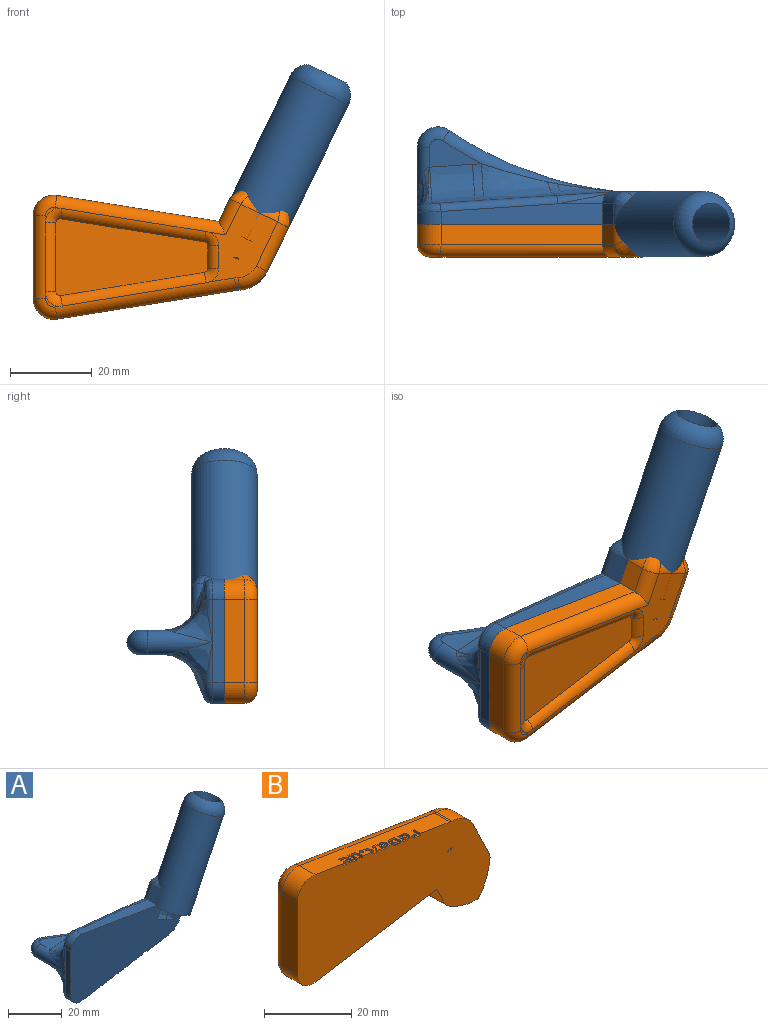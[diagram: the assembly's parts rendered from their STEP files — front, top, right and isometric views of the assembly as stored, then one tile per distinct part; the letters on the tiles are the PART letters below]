
ASSEMBLY  parts=2 mates=1
PART A: 139 faces, bbox 79.2x33.1x63.6 mm
  f0: plane 59.38x33.12mm, normal (0,-1,0), area 1204.5mm2, adj f1,f2,f3,f10,f11,f12,f17,f18
  f1: plane 43.87x7.02mm, normal (0.16,0,-0.99), area 174.7mm2, adj f0,f12,f14,f21,f29,f70,f71,f72
  f2: plane 0.98x0.28mm, normal (0.16,0,-0.99), area 0.2mm2, adj f0,f79,f80,f81,f82
  f3: plane 1.13x0.48mm, normal (0.16,0,-0.99), area 0.4mm2, adj f0,f74,f75,f76,f77
  f4: plane 13.96x9.51mm, normal (-0.07,1,0), area 24.1mm2, adj f28,f30,f32,f45
  f5: plane 10.96x6.39mm, normal (-0.07,1,0), area 12.6mm2, adj f9,f31,f33,f55
  f6: plane 18.19x10.63mm, normal (0,1,0), area 119mm2, adj f9,f13,f15,f22,f23,f32,f49,f51
  f7: plane 8.12x0.95mm, normal (-0.07,1,0), area 4.2mm2, adj f27,f29,f52,f54
  f8: cylinder r=2mm len=20.37mm, axis (0,0,-1), area 22.6mm2, adj f11,f25,f27,f46,f48
  f9: cylinder r=2mm len=3.69mm, axis (0,0,-1), area 0.4mm2, adj f5,f6,f33,f53
  f10: cylinder r=5mm len=5.8mm, axis (0,1,0), area 26mm2, adj f0,f11,f20,f25
  f11: plane 20.37x2.88mm, normal (-1,0,0), area 58.7mm2, adj f0,f8,f10,f12
  f12: cylinder r=5mm len=5.79mm, axis (0,1,0), area 25.9mm2, adj f0,f1,f11,f27
  f13: torus R=8mm, axis (0,-1,0), area 3.6mm2, adj f6,f14,f21,f23,f33
  f14: cylinder r=3mm len=15.67mm, axis (0.99,0,0.16), area 26.4mm2, adj f1,f13,f31
  f15: cylinder r=3mm len=7.86mm, axis (-0.44,0,-0.9), area 27.9mm2, adj f6,f16,f19,f28,f30,f60
  f16: cylinder r=3mm len=11.93mm, axis (-0.99,0,0.16), area 14.6mm2, adj f15,f20,f28
  f17: cylinder r=8mm len=6.92mm, axis (0,1,0), area 43.3mm2, adj f0,f18,f21,f23
  f18: plane 10.79x5.26mm, normal (0.9,0,-0.44), area 60mm2, adj f0,f17,f22,f63,f64
  f19: plane 5.54x5mm, normal (-0.9,0,0.44), area 30.8mm2, adj f15,f20,f59,f64
  f20: plane 39.57x6.41mm, normal (0.16,0,0.99), area 173.1mm2, adj f0,f10,f16,f19,f26
  f21: cylinder r=5mm len=5mm, axis (0,1,0), area 3.1mm2, adj f0,f1,f13,f17
  f22: cylinder r=3mm len=12.1mm, axis (0.44,0,0.9), area 56.5mm2, adj f6,f18,f23,f62
  f23: torus R=5mm, axis (0,-1,0), area 35.3mm2, adj f6,f13,f17,f22
  f24: plane 11.83x1.53mm, normal (-0.07,1,0), area 9.6mm2, adj f25,f26,f40,f42
  f25: bspline ~6.51x5.22mm, area 22mm2, adj f8,f10,f24,f26,f44
  f26: cylinder r=2mm len=29.07mm, axis (0.99,0.06,-0.16), area 91.9mm2, adj f20,f24,f25,f28,f39,f41
  f27: bspline ~6.51x5.87mm, area 21.3mm2, adj f7,f8,f12,f29,f50
  f28: bspline ~18.15x6.04mm, area 28.9mm2, adj f4,f15,f16,f26,f30,f43
  f29: cylinder r=2mm len=29.07mm, axis (0.99,0.06,0.16), area 91.9mm2, adj f1,f7,f27,f31,f56,f58
  f30: bspline ~4.02x3.48mm, area 2.9mm2, adj f4,f15,f28,f32
  f31: bspline ~17.8x6.19mm, area 31.6mm2, adj f5,f14,f29,f33,f57
  f32: cylinder r=2mm len=8.96mm, axis (0,0,-1), area 1.1mm2, adj f4,f6,f30,f47
  f33: bspline ~0.55x0.32mm, area 0mm2, adj f5,f9,f13,f31
  f34: plane 12.78x6.91mm, normal (0,0,-1), area 49mm2, adj f36,f37,f38,f54,f56
  f35: plane 12.67x6.86mm, normal (0,0,1), area 48.9mm2, adj f36,f37,f38,f39,f40
  f36: torus R=91.5mm, axis (0,0,1), area 273.7mm2, adj f34,f35,f37,f41,f43,f45,f47,f49
  f37: torus R=2mm, axis (0,0,1), area 79.9mm2, adj f34,f35,f36,f38
  f38: cylinder r=3mm len=15.5mm, axis (0,1,0), area 82.4mm2, adj f34,f35,f37,f42,f44,f46,f48,f50
  f39: bspline ~9.12x9mm, area 29.9mm2, adj f26,f35,f40,f41
  f40: bspline ~13.25x9.82mm, area 147.7mm2, adj f24,f35,f39,f42
  f41: bspline ~18.28x9.37mm, area 170.8mm2, adj f26,f36,f39,f43
  f42: bspline ~9.07x9.02mm, area 10mm2, adj f24,f38,f40,f44
  f43: bspline ~6.69x4.69mm, area 18.2mm2, adj f28,f36,f41,f45
  f44: bspline ~9.31x9.21mm, area 9.7mm2, adj f25,f38,f42,f46
  f45: bspline ~20.74x9.64mm, area 66.6mm2, adj f4,f36,f43,f47
  f46: bspline ~10.45x9.78mm, area 44.9mm2, adj f8,f38,f44,f48
  f47: bspline ~1.74x1.66mm, area 1.2mm2, adj f32,f36,f45,f49
  f48: bspline ~9.91x9.29mm, area 41.2mm2, adj f8,f38,f46,f50
  f49: bspline ~1.5x1.17mm, area 1mm2, adj f6,f36,f47,f51
  f50: bspline ~9.49x9.33mm, area 16.1mm2, adj f27,f38,f48,f52
  f51: bspline ~1.5x1.17mm, area 1mm2, adj f6,f36,f49,f53
  f52: bspline ~9.04x9.01mm, area 6.8mm2, adj f7,f38,f50,f54
  f53: bspline ~1.74x1.66mm, area 1.2mm2, adj f9,f36,f51,f55
  f54: bspline ~13.25x9.82mm, area 101.4mm2, adj f7,f34,f52,f56
  f55: bspline ~20.69x9.63mm, area 47.8mm2, adj f5,f36,f53,f57
  f56: bspline ~9.3x9mm, area 74.3mm2, adj f29,f34,f54,f58
  f57: bspline ~7.28x6.44mm, area 34.3mm2, adj f31,f36,f55,f58
  f58: bspline ~18.22x8.95mm, area 163mm2, adj f29,f36,f56,f57
  f59: bspline ~10.7x7.19mm, area 5.6mm2, adj f19,f60,f64
  f60: bspline ~4.49x3.76mm, area 13.9mm2, adj f15,f59,f61,f64
  f61: bspline ~12.5x11.57mm, area 11.6mm2, adj f6,f60,f62,f64
  f62: bspline ~3.91x3.76mm, area 13.9mm2, adj f22,f61,f63,f64
  f63: bspline ~10.7x7.19mm, area 5.6mm2, adj f18,f62,f64
  f64: cylinder r=8mm len=43.38mm, axis (0.44,0,0.9), area 1816.7mm2, adj f0,f18,f19,f59,f60,f61,f62,f63
  f65: plane 14.38x8mm, normal (-0.44,0,-0.9), area 59.7mm2, adj f0,f64,f66
  f66: cylinder r=5.1mm len=49.41mm, axis (0.44,0,0.9), area 1522.1mm2, adj f0,f65,f68,f69
  f67: cylinder r=0.02mm len=17.99mm, axis (0.44,0,0.9), area 1mm2, adj f0,f68
  f68: plane 9.17x5.1mm, normal (0.44,0,0.9), area 40.8mm2, adj f0,f66,f67
  f69: torus R=3mm, axis (0.44,0,0.9), area 249.7mm2, adj f64,f66
  f70: extruded ~0.7x0.55mm, area 0.4mm2, adj f0,f1,f71,f78
  f71: extruded ~1.07x0.65mm, area 0.5mm2, adj f1,f70,f72,f78
  f72: extruded ~1.12x0.66mm, area 0.6mm2, adj f1,f71,f73,f78
  f73: extruded ~0.65x0.55mm, area 0.4mm2, adj f0,f1,f72,f78
  f74: extruded ~0.56x0.49mm, area 0.2mm2, adj f3,f75,f77,f78
  f75: extruded ~0.56x0.49mm, area 0.2mm2, adj f3,f74,f76,f78
  f76: extruded ~0.52x0.31mm, area 0.2mm2, adj f0,f3,f75,f78
  f77: extruded ~0.52x0.31mm, area 0.2mm2, adj f0,f3,f74,f78
  f78: plane 2.72x1.09mm, normal (0.16,0,-0.99), area 1.8mm2, adj f0,f70,f71,f72,f73,f74,f75,f76
  f79: extruded ~0.5x0.11mm, area 0mm2, adj f0,f2,f80,f91
  f80: extruded ~0.56x0.5mm, area 0.3mm2, adj f2,f79,f81,f91
  f81: extruded ~0.57x0.56mm, area 0.3mm2, adj f2,f80,f82,f91
  f82: extruded ~0.5x0.12mm, area 0mm2, adj f0,f2,f81,f91
  f83: plane 2.08x0.49mm, normal (0.99,0,0.16), area 1mm2, adj f0,f1,f84,f91
  f84: plane 0.9x0.63mm, normal (0,-1,0), area 0.4mm2, adj f1,f83,f85,f91
  f85: plane 0.97x0.49mm, normal (-0.99,0,-0.16), area 0.5mm2, adj f1,f84,f86,f91
  f86: extruded ~0.61x0.5mm, area 0.3mm2, adj f1,f85,f87,f91
  f87: plane 0.5x0.11mm, normal (0,-1,0), area 0mm2, adj f1,f86,f88,f91
  f88: extruded ~0.94x0.63mm, area 0.5mm2, adj f1,f87,f89,f91
  f89: extruded ~0.92x0.63mm, area 0.5mm2, adj f1,f88,f90,f91
  f90: extruded ~0.54x0.53mm, area 0.3mm2, adj f0,f1,f89,f91
  f91: plane 2.74x2.1mm, normal (0.16,0,-0.99), area 3mm2, adj f0,f79,f80,f81,f82,f83,f84,f85
  f92: plane 1.97x1.31mm, normal (0.83,0.53,0.13), area 1.2mm2, adj f0,f1,f93,f99
  f93: plane 0.97x0.64mm, normal (0,-1,0), area 0.5mm2, adj f1,f92,f94,f99
  f94: plane 1.43x0.91mm, normal (-0.85,-0.51,-0.14), area 0.8mm2, adj f1,f93,f95,f99
  f95: plane 1.43x0.92mm, normal (0.85,-0.51,0.14), area 0.8mm2, adj f1,f94,f96,f99
  f96: plane 1x0.64mm, normal (0,-1,0), area 0.5mm2, adj f1,f95,f97,f99
  f97: plane 1.92x1.3mm, normal (-0.83,0.54,-0.13), area 1.1mm2, adj f1,f96,f98,f99
  f98: plane 0.5x0.11mm, normal (-0.83,-0.54,-0.13), area 0mm2, adj f0,f1,f97,f99
  f99: plane 3.48x1.97mm, normal (0.16,0,-0.99), area 3.3mm2, adj f0,f92,f93,f94,f95,f96,f97,f98
  f100: extruded ~0.8x0.55mm, area 0.4mm2, adj f0,f1,f101,f106
  f101: extruded ~1x0.64mm, area 0.5mm2, adj f1,f100,f102,f106
  f102: extruded ~1.23x0.68mm, area 0.6mm2, adj f1,f101,f103,f106
  f103: plane 0.56x0.54mm, normal (-0.89,0.44,-0.14), area 0.3mm2, adj f1,f102,f104,f106
  f104: extruded ~0.92x0.63mm, area 0.4mm2, adj f1,f103,f105,f106
  f105: extruded ~0.57x0.55mm, area 0.4mm2, adj f0,f1,f104,f106
  f106: plane 2.39x1.07mm, normal (0.16,0,-0.99), area 1.6mm2, adj f0,f100,f101,f102,f103,f104,f105
  f107: plane 0.57x0.56mm, normal (0,-1,0), area 0.2mm2, adj f108,f120,f122,f123
  f108: plane 0.88x0.49mm, normal (0.99,0,0.16), area 0.4mm2, adj f107,f109,f122,f123
  f109: plane 0.56x0.52mm, normal (0,1,0), area 0.2mm2, adj f108,f110,f122,f123
  f110: extruded ~0.6x0.58mm, area 0.3mm2, adj f109,f111,f122,f123
  f111: extruded ~0.52x0.33mm, area 0.2mm2, adj f110,f112,f122,f123
  f112: extruded ~0.52x0.35mm, area 0.2mm2, adj f111,f120,f122,f123
  f113: plane 1.3x0.69mm, normal (0,-1,0), area 0.6mm2, adj f1,f114,f121,f122
  f114: plane 1.97x0.49mm, normal (-0.99,0,-0.16), area 1mm2, adj f0,f1,f113,f122
  f115: extruded ~0.53x0.32mm, area 0.1mm2, adj f0,f1,f116,f122
  f116: plane 0.49x0.08mm, normal (0.99,0,0.16), area 0mm2, adj f1,f115,f117,f122
  f117: extruded ~0.56x0.52mm, area 0.3mm2, adj f1,f116,f118,f122
  f118: extruded ~0.58x0.52mm, area 0.3mm2, adj f1,f117,f119,f122
  f119: extruded ~0.76x0.55mm, area 0.4mm2, adj f1,f118,f121,f122
  f120: extruded ~0.57x0.57mm, area 0.3mm2, adj f107,f112,f122,f123
  f121: extruded ~1.29x0.69mm, area 0.6mm2, adj f1,f113,f119,f122
  f122: plane 2.8x1.97mm, normal (0.16,0,-0.99), area 4.3mm2, adj f0,f107,f108,f109,f110,f111,f112,f113
  f123: plane 1.12x0.88mm, normal (0.16,0,-0.99), area 0.9mm2, adj f107,f108,f109,f110,f111,f112,f120
  f124: extruded ~0.8x0.55mm, area 0.4mm2, adj f0,f1,f125,f130
  f125: extruded ~1x0.64mm, area 0.5mm2, adj f1,f124,f126,f130
  f126: extruded ~1.23x0.68mm, area 0.6mm2, adj f1,f125,f127,f130
  f127: plane 0.56x0.54mm, normal (-0.89,0.44,-0.14), area 0.3mm2, adj f1,f126,f128,f130
  f128: extruded ~0.92x0.63mm, area 0.4mm2, adj f1,f127,f129,f130
  f129: extruded ~0.57x0.55mm, area 0.4mm2, adj f0,f1,f128,f130
  f130: plane 2.39x1.07mm, normal (0.16,0,-0.99), area 1.6mm2, adj f0,f124,f125,f126,f127,f128,f129
  f131: plane 0.49x0.25mm, normal (0.99,0,0.16), area 0.1mm2, adj f0,f1,f132,f138
  f132: plane 1.41x0.71mm, normal (0,-1,0), area 0.7mm2, adj f1,f131,f133,f138
  f133: plane 1.02x0.49mm, normal (0.99,0,0.16), area 0.5mm2, adj f1,f132,f134,f138
  f134: plane 1.51x0.72mm, normal (0,1,0), area 0.7mm2, adj f1,f133,f135,f138
  f135: plane 0.69x0.49mm, normal (0.99,0,0.16), area 0.3mm2, adj f1,f134,f136,f138
  f136: plane 2.32x0.85mm, normal (0,-1,0), area 1.1mm2, adj f1,f135,f137,f138
  f137: plane 1.97x0.49mm, normal (-0.99,0,-0.16), area 1mm2, adj f0,f1,f136,f138
  f138: plane 2.25x1.97mm, normal (0.16,0,-0.99), area 3mm2, adj f0,f131,f132,f133,f134,f135,f136,f137
PART B: 157 faces, bbox 68x10.3x38.8 mm
  f0: plane 43.85x7.11mm, normal (0.16,0,0.99), area 191.2mm2, adj f3,f11,f12,f21,f36,f37,f38,f39
  f1: plane 1.15x0.19mm, normal (0.16,0,0.99), area 0.2mm2, adj f3,f48,f49,f50
  f2: plane 1.55x1.21mm, normal (0.16,0,0.99), area 1.7mm2, adj f3,f53,f54,f55,f56,f57,f58,f67
  f3: plane 64.71x35.47mm, normal (0,-1,0), area 1448.9mm2, adj f0,f1,f2,f7,f8,f9,f10,f11
  f4: plane 3.23x2.92mm, normal (0,1,0), area 2mm2, adj f23,f25,f26,f34
  f5: plane 19.06x16.66mm, normal (0,1,0), area 170.7mm2, adj f7,f8,f17,f18,f19,f20,f21,f24
  f6: plane 3.24x2.93mm, normal (0,1,0), area 2.1mm2, adj f21,f22,f23,f30
  f7: plane 8x1.31mm, normal (0.39,0,-0.92), area 11.4mm2, adj f3,f5,f8,f17
  f8: plane 8x0.56mm, normal (-0.9,0,0.44), area 5mm2, adj f3,f5,f7,f17
  f9: plane 10.79x5.26mm, normal (0.9,0,0.44), area 60mm2, adj f3,f10,f18,f152
  f10: cylinder r=8mm len=6.91mm, axis (0,1,0), area 43.3mm2, adj f3,f9,f11,f19
  f11: cylinder r=5mm len=5mm, axis (0,1,0), area 3.2mm2, adj f0,f3,f10,f20
  f12: cylinder r=5mm len=5.8mm, axis (0,1,0), area 43.3mm2, adj f0,f3,f13,f22
  f13: plane 20.37x5mm, normal (-1,0,0), area 101.8mm2, adj f3,f12,f14,f23
  f14: cylinder r=5mm len=5.79mm, axis (0,1,0), area 43.2mm2, adj f3,f13,f15,f25
  f15: plane 39.57x6.33mm, normal (0.16,0,-0.99), area 200.4mm2, adj f3,f14,f16,f26
  f16: plane 5.55x5mm, normal (-0.9,0,-0.44), area 30.9mm2, adj f3,f15,f24,f156
  f17: plane 8x1.04mm, normal (0,0,1), area 8.3mm2, adj f3,f5,f7,f8
  f18: cylinder r=3mm len=12.1mm, axis (-0.44,0,0.9), area 56.5mm2, adj f5,f9,f19,f153
  f19: torus R=5mm, axis (0,-1,0), area 35.2mm2, adj f5,f10,f18,f20
  f20: torus R=8mm, axis (0,-1,0), area 3.6mm2, adj f5,f11,f19,f21
  f21: cylinder r=3mm len=44.33mm, axis (-0.99,0,0.16), area 207.5mm2, adj f0,f5,f6,f20,f22,f28,f29,f30
  f22: torus R=2mm, axis (0,-1,0), area 31.9mm2, adj f6,f12,f21,f23
  f23: cylinder r=3mm len=20.37mm, axis (0,0,-1), area 95.1mm2, adj f4,f6,f13,f22,f25,f30,f32,f34
  f24: cylinder r=3mm len=8.86mm, axis (0.44,0,-0.9), area 34.3mm2, adj f5,f16,f26,f155
  f25: torus R=2mm, axis (0,-1,0), area 31.9mm2, adj f4,f14,f23,f26
  f26: cylinder r=3mm len=42.24mm, axis (0.99,0,0.16), area 190.9mm2, adj f4,f5,f15,f24,f25,f33,f34,f35
  f27: plane 37.22x18.84mm, normal (0,1,0), area 490.3mm2, adj f28,f29,f30,f31,f32,f33,f34,f35
  f28: cylinder r=3mm len=35.63mm, axis (-0.99,0,0.16), area 110.3mm2, adj f21,f27,f29,f30
  f29: torus R=3.6mm, axis (0,-1,0), area 9.6mm2, adj f5,f21,f27,f28,f31
  f30: torus R=3.6mm, axis (0,-1,0), area 11.7mm2, adj f6,f21,f23,f27,f28,f32
  f31: cylinder r=3mm len=5.5mm, axis (0,0,-1), area 17.3mm2, adj f5,f27,f29,f33
  f32: cylinder r=3mm len=16.84mm, axis (0,0,-1), area 52.1mm2, adj f23,f27,f30,f34
  f33: torus R=3.6mm, axis (0,-1,0), area 9.6mm2, adj f5,f26,f27,f31,f35
  f34: torus R=3.6mm, axis (0,-1,0), area 11.7mm2, adj f4,f23,f26,f27,f32,f35
  f35: cylinder r=3mm len=35.63mm, axis (-0.99,0,-0.16), area 110.3mm2, adj f26,f27,f33,f34
  f36: extruded ~1.21x0.68mm, area 0.6mm2, adj f0,f37,f51,f52
  f37: extruded ~0.67x0.59mm, area 0.3mm2, adj f0,f36,f38,f52
  f38: extruded ~0.57x0.54mm, area 0.2mm2, adj f0,f37,f39,f52
  f39: plane 0.64x0.49mm, normal (0.99,0,-0.16), area 0.3mm2, adj f0,f38,f40,f52
  f40: extruded ~0.58x0.58mm, area 0.3mm2, adj f0,f39,f41,f52
  f41: extruded ~0.59x0.58mm, area 0.3mm2, adj f0,f40,f42,f52
  f42: extruded ~0.62x0.58mm, area 0.3mm2, adj f0,f41,f43,f52
  f43: extruded ~0.55x0.53mm, area 0.3mm2, adj f0,f42,f44,f52
  f44: plane 2.01x0.81mm, normal (0,-1,0), area 1mm2, adj f0,f43,f45,f52
  f45: plane 0.49x0.4mm, normal (0.99,0,-0.16), area 0.2mm2, adj f0,f44,f46,f52
  f46: extruded ~0.5x0.32mm, area 0.2mm2, adj f0,f3,f45,f52
  f47: extruded ~0.53x0.5mm, area 0.3mm2, adj f0,f3,f51,f52
  f48: extruded ~0.5x0.17mm, area 0.1mm2, adj f1,f3,f49,f52
  f49: plane 1.23x0.68mm, normal (0,1,0), area 0.6mm2, adj f1,f48,f50,f52
  f50: extruded ~0.5x0.17mm, area 0.1mm2, adj f1,f3,f49,f52
  f51: extruded ~1.15x0.56mm, area 0.6mm2, adj f0,f36,f47,f52
  f52: plane 2.76x2.09mm, normal (0.16,0,0.99), area 3.7mm2, adj f3,f36,f37,f38,f39,f40,f41,f42
  f53: extruded ~0.57x0.54mm, area 0.3mm2, adj f2,f54,f67,f68
  f54: extruded ~0.56x0.52mm, area 0.3mm2, adj f2,f53,f55,f68
  f55: extruded ~0.67x0.52mm, area 0.3mm2, adj f2,f54,f56,f68
  f56: extruded ~0.64x0.51mm, area 0.3mm2, adj f2,f3,f55,f68
  f57: extruded ~0.63x0.51mm, area 0.3mm2, adj f2,f3,f58,f68
  f58: plane 0.49x0.09mm, normal (-0.99,0,0.16), area 0mm2, adj f2,f57,f67,f68
  f59: extruded ~0.91x0.63mm, area 0.5mm2, adj f0,f60,f66,f68
  f60: extruded ~0.93x0.63mm, area 0.5mm2, adj f0,f59,f61,f68
  f61: plane 0.5x0.12mm, normal (0,-1,0), area 0mm2, adj f0,f60,f62,f68
  f62: plane 0.52x0.39mm, normal (-0.91,-0.38,0.15), area 0.2mm2, adj f0,f61,f63,f68
  f63: plane 0.71x0.6mm, normal (0,-1,0), area 0.3mm2, adj f0,f62,f64,f68
  f64: plane 2.14x0.49mm, normal (0.99,0,-0.16), area 1.1mm2, adj f0,f3,f63,f68
  f65: extruded ~0.63x0.5mm, area 0.3mm2, adj f0,f3,f66,f68
  f66: extruded ~1.15x0.54mm, area 0.6mm2, adj f0,f59,f65,f68
  f67: extruded ~0.63x0.52mm, area 0.3mm2, adj f2,f53,f58,f68
  f68: plane 2.8x2.21mm, normal (0.16,0,0.99), area 4mm2, adj f3,f53,f54,f55,f56,f57,f58,f59
  f69: plane 1.03x0.65mm, normal (0,-1,0), area 0.5mm2, adj f0,f70,f75,f76
  f70: plane 2x1.4mm, normal (0.82,0.56,-0.13), area 1.2mm2, adj f0,f69,f71,f76
  f71: plane 0.49x0.08mm, normal (0.83,-0.53,-0.14), area 0mm2, adj f0,f3,f70,f76
  f72: plane 2x1.35mm, normal (-0.83,0.54,0.13), area 1.2mm2, adj f0,f3,f73,f76
  f73: plane 0.97x0.64mm, normal (0,-1,0), area 0.5mm2, adj f0,f72,f74,f76
  f74: plane 1.5x0.99mm, normal (0.84,-0.52,-0.14), area 0.9mm2, adj f0,f73,f75,f76
  f75: plane 1.5x0.99mm, normal (-0.84,-0.52,0.14), area 0.9mm2, adj f0,f69,f74,f76
  f76: plane 3.66x2mm, normal (0.16,0,0.99), area 3.4mm2, adj f3,f69,f70,f71,f72,f73,f74,f75
  f77: plane 0.55x0.4mm, normal (0.03,-1,-0.01), area 0.2mm2, adj f78,f97,f98,f149
  f78: plane 0.49x0.25mm, normal (-0.99,0,0.16), area 0.1mm2, adj f77,f79,f98,f149
  f79: extruded ~0.52x0.44mm, area 0.2mm2, adj f78,f80,f98,f149
  f80: extruded ~0.57x0.53mm, area 0.3mm2, adj f79,f81,f98,f149
  f81: extruded ~0.56x0.48mm, area 0.3mm2, adj f80,f82,f98,f149
  f82: extruded ~0.52x0.36mm, area 0.2mm2, adj f81,f97,f98,f149
  f83: plane 0.52x0.41mm, normal (-0.92,-0.36,0.15), area 0.2mm2, adj f0,f84,f96,f98
  f84: plane 0.65x0.59mm, normal (0,-1,0), area 0.3mm2, adj f0,f83,f85,f98
  f85: plane 2.02x0.49mm, normal (0.99,0,-0.16), area 1mm2, adj f0,f84,f86,f98
  f86: extruded ~0.49x0.08mm, area 0mm2, adj f0,f3,f85,f98
  f87: extruded ~0.49x0.08mm, area 0mm2, adj f0,f3,f88,f98
  f88: plane 0.49x0.13mm, normal (-0.99,0,0.16), area 0.1mm2, adj f0,f87,f89,f98
  f89: plane 0.6x0.58mm, normal (-0.03,1,0.01), area 0.3mm2, adj f0,f88,f90,f98
  f90: extruded ~1.09x0.66mm, area 0.5mm2, adj f0,f89,f91,f98
  f91: extruded ~0.71x0.55mm, area 0.4mm2, adj f0,f90,f92,f98
  f92: extruded ~0.71x0.53mm, area 0.4mm2, adj f0,f91,f93,f98
  f93: extruded ~0.76x0.6mm, area 0.4mm2, adj f0,f92,f94,f98
  f94: extruded ~0.65x0.59mm, area 0.3mm2, adj f0,f93,f95,f98
  f95: extruded ~0.56x0.5mm, area 0.3mm2, adj f0,f94,f96,f98
  f96: plane 0.5x0.1mm, normal (0,-1,0), area 0mm2, adj f0,f83,f95,f98
  f97: extruded ~0.61x0.58mm, area 0.3mm2, adj f77,f82,f98,f149
  f98: plane 2.67x2.08mm, normal (0.16,0,0.99), area 4mm2, adj f3,f77,f78,f79,f80,f81,f82,f83
  f99: plane 1.03x0.49mm, normal (0.99,0,-0.16), area 0.5mm2, adj f100,f110,f111,f150
  f100: plane 0.59x0.58mm, normal (0,-1,0), area 0.3mm2, adj f99,f101,f111,f150
  f101: extruded ~0.78x0.61mm, area 0.5mm2, adj f100,f102,f111,f150
  f102: extruded ~0.52x0.41mm, area 0.2mm2, adj f101,f103,f111,f150
  f103: extruded ~0.59x0.58mm, area 0.3mm2, adj f102,f110,f111,f150
  f104: plane 2x0.49mm, normal (-0.99,0,0.16), area 1mm2, adj f0,f3,f105,f111
  f105: plane 1.54x0.73mm, normal (0,-1,0), area 0.7mm2, adj f0,f104,f106,f111
  f106: extruded ~1.13x0.66mm, area 0.6mm2, adj f0,f105,f107,f111
  f107: extruded ~0.85x0.56mm, area 0.5mm2, adj f0,f106,f108,f111
  f108: extruded ~0.61x0.52mm, area 0.3mm2, adj f0,f107,f109,f111
  f109: extruded ~0.54x0.38mm, area 0.2mm2, adj f0,f3,f108,f111
  f110: plane 0.62x0.58mm, normal (0,1,0), area 0.3mm2, adj f99,f103,f111,f150
  f111: plane 2.9x2.01mm, normal (0.16,0,0.99), area 4.3mm2, adj f3,f99,f100,f101,f102,f103,f104,f105
  f112: plane 0.55x0.4mm, normal (0.03,-1,-0.01), area 0.2mm2, adj f113,f132,f133,f151
  f113: plane 0.49x0.25mm, normal (-0.99,0,0.16), area 0.1mm2, adj f112,f114,f133,f151
  f114: extruded ~0.52x0.44mm, area 0.2mm2, adj f113,f115,f133,f151
  f115: extruded ~0.57x0.53mm, area 0.3mm2, adj f114,f116,f133,f151
  f116: extruded ~0.56x0.48mm, area 0.3mm2, adj f115,f117,f133,f151
  f117: extruded ~0.52x0.36mm, area 0.2mm2, adj f116,f132,f133,f151
  f118: plane 0.52x0.41mm, normal (-0.92,-0.36,0.15), area 0.2mm2, adj f0,f119,f131,f133
  f119: plane 0.65x0.59mm, normal (0,-1,0), area 0.3mm2, adj f0,f118,f120,f133
  f120: plane 2.02x0.49mm, normal (0.99,0,-0.16), area 1mm2, adj f0,f119,f121,f133
  f121: extruded ~0.49x0.08mm, area 0mm2, adj f0,f3,f120,f133
  f122: extruded ~0.49x0.08mm, area 0mm2, adj f0,f3,f123,f133
  f123: plane 0.49x0.13mm, normal (-0.99,0,0.16), area 0.1mm2, adj f0,f122,f124,f133
  f124: plane 0.6x0.58mm, normal (-0.03,1,0.01), area 0.3mm2, adj f0,f123,f125,f133
  f125: extruded ~1.09x0.66mm, area 0.5mm2, adj f0,f124,f126,f133
  f126: extruded ~0.71x0.55mm, area 0.4mm2, adj f0,f125,f127,f133
  f127: extruded ~0.71x0.53mm, area 0.4mm2, adj f0,f126,f128,f133
  f128: extruded ~0.76x0.6mm, area 0.4mm2, adj f0,f127,f129,f133
  f129: extruded ~0.65x0.59mm, area 0.3mm2, adj f0,f128,f130,f133
  f130: extruded ~0.56x0.5mm, area 0.3mm2, adj f0,f129,f131,f133
  f131: plane 0.5x0.1mm, normal (0,-1,0), area 0mm2, adj f0,f118,f130,f133
  f132: extruded ~0.61x0.58mm, area 0.3mm2, adj f112,f117,f133,f151
  f133: plane 2.67x2.08mm, normal (0.16,0,0.99), area 4mm2, adj f3,f112,f113,f114,f115,f116,f117,f118
  f134: plane 0.9x0.63mm, normal (0,-1,0), area 0.4mm2, adj f0,f135,f138,f139
  f135: plane 1.57x0.49mm, normal (0.99,0,-0.16), area 0.8mm2, adj f0,f134,f136,f139
  f136: plane 1.41x0.71mm, normal (0,-1,0), area 0.7mm2, adj f0,f135,f137,f139
  f137: plane 0.49x0.43mm, normal (0.99,0,-0.16), area 0.2mm2, adj f0,f3,f136,f139
  f138: plane 2x0.49mm, normal (-0.99,0,0.16), area 1mm2, adj f0,f3,f134,f139
  f139: plane 2.14x2mm, normal (0.16,0,0.99), area 2.2mm2, adj f3,f134,f135,f136,f137,f138
  f140: extruded ~0.51x0.34mm, area 0.2mm2, adj f0,f141,f147,f148
  f141: extruded ~0.51x0.34mm, area 0.2mm2, adj f0,f140,f142,f148
  f142: extruded ~0.55x0.43mm, area 0.2mm2, adj f0,f141,f143,f148
  f143: extruded ~0.55x0.42mm, area 0.2mm2, adj f0,f142,f144,f148
  f144: extruded ~0.51x0.34mm, area 0.2mm2, adj f0,f143,f145,f148
  f145: extruded ~0.51x0.34mm, area 0.2mm2, adj f0,f144,f146,f148
  f146: extruded ~0.55x0.42mm, area 0.2mm2, adj f0,f145,f147,f148
  f147: extruded ~0.55x0.43mm, area 0.2mm2, adj f0,f140,f146,f148
  f148: plane 0.94x0.92mm, normal (0.16,0,0.99), area 0.7mm2, adj f140,f141,f142,f143,f144,f145,f146,f147
  f149: plane 1.02x0.86mm, normal (0.16,0,0.99), area 0.7mm2, adj f77,f78,f79,f80,f81,f82,f97
  f150: plane 1.21x1.03mm, normal (0.16,0,0.99), area 1.1mm2, adj f99,f100,f101,f102,f103,f110
  f151: plane 1.02x0.86mm, normal (0.16,0,0.99), area 0.7mm2, adj f112,f113,f114,f115,f116,f117,f132
  f152: bspline ~10.7x7.19mm, area 29.3mm2, adj f3,f9,f153
  f153: bspline ~10.7x8mm, area 22.8mm2, adj f18,f152,f154
  f154: bspline ~12.5x11.57mm, area 58.6mm2, adj f5,f153,f155
  f155: bspline ~10.7x8mm, area 22.8mm2, adj f24,f154,f156
  f156: bspline ~10.7x7.19mm, area 29.3mm2, adj f3,f16,f155
PLACE A t=(0,5.71,-0.67)mm
PLACE B rot(axis=(1,0,0),180deg) t=(0,-10.29,-6.13)mm
MATE fastened A.f0 <-> B.f3  axis (0,-1,0) through (-16.6,-2.29,-3.4)mm
